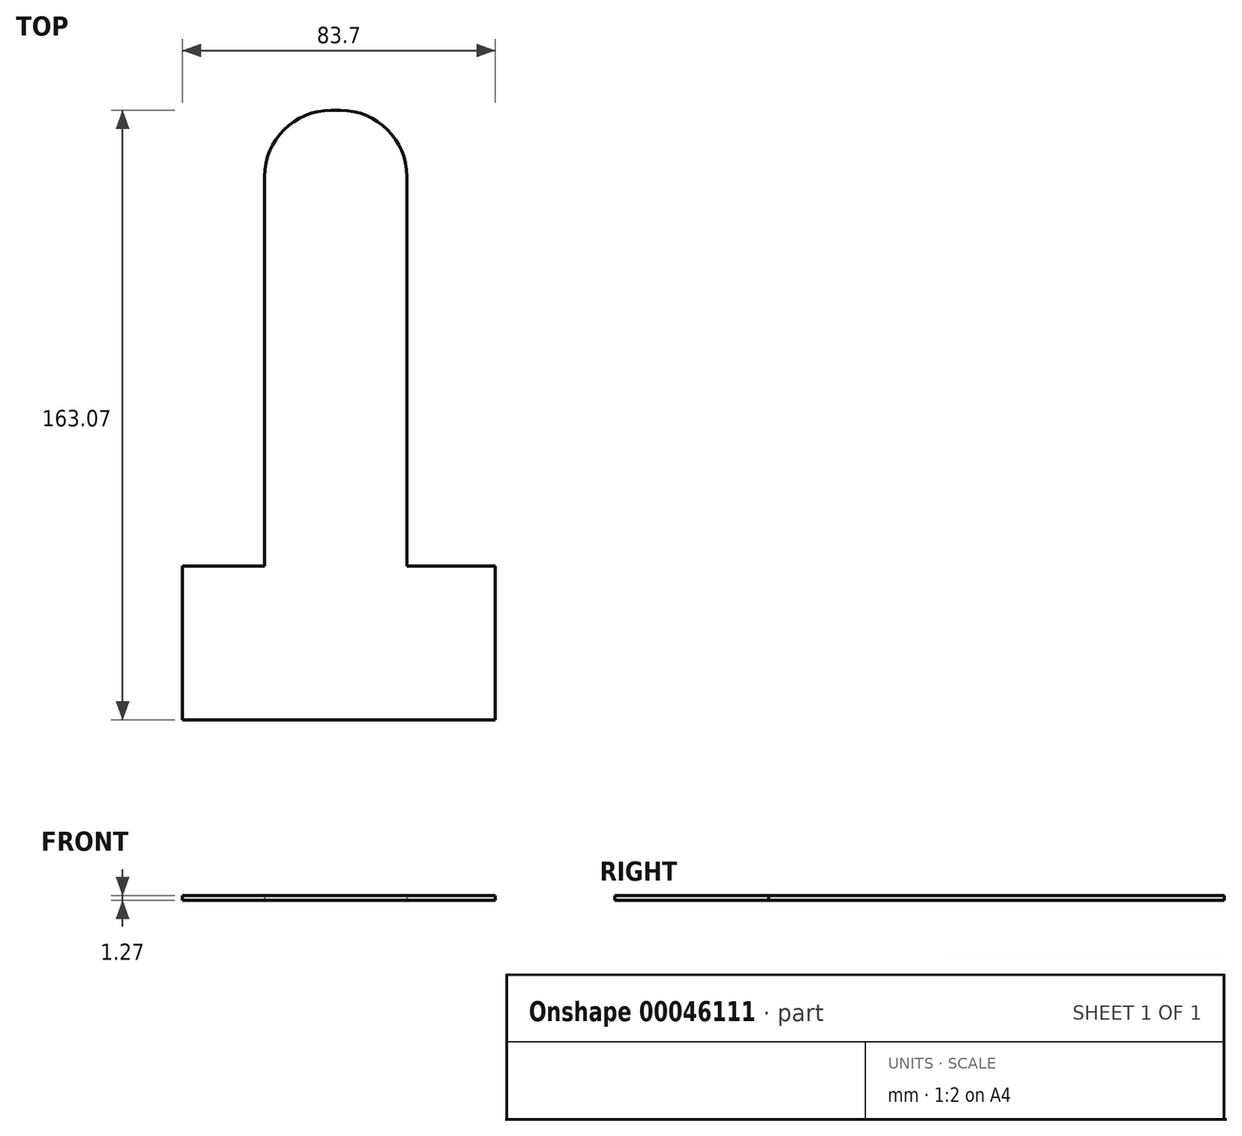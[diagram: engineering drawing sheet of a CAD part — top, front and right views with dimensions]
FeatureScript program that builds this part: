
annotation { "Feature Type Name" : "Feature", "Feature Type Description" : "" }
export const myFeature = defineFeature(function(context is Context, id is Id, definition is map)
    precondition{}
    {
        {
            var Q0;
            Q0=qCreatedBy(makeId("Top.planeOp"),FACE);
            var sketch = newSketch(context, id + "F0", { "sketchPlane" : qUnion([Q0])});
            skLineSegment(sketch, "E0", {"start": v(-41.7, -21.85) * mm, "end": v(42, -21.85) * mm});
            skLineSegment(sketch, "E1", {"start": v(-19.71, 141.22) * mm, "end": v(-19.71, 19.3) * mm});
            skLineSegment(sketch, "E2", {"start": v(18.39, 19.3) * mm, "end": v(18.39, 141.22) * mm});
            skLineSegment(sketch, "E3", {"start": v(18.39, 141.22) * mm, "end": v(-19.71, 141.22) * mm});
            skLineSegment(sketch, "E4", {"start": v(-41.7, -21.85) * mm, "end": v(-41.7, 19.3) * mm});
            skLineSegment(sketch, "E5", {"start": v(42, 19.3) * mm, "end": v(42, -21.85) * mm});
            skLineSegment(sketch, "E6", {"start": v(-41.7, 19.3) * mm, "end": v(-19.71, 19.3) * mm});
            skLineSegment(sketch, "E7", {"start": v(18.39, 19.3) * mm, "end": v(42, 19.3) * mm});
            skSolve(sketch);
        }
        {
            var Q0;
            Q0 = qSketchRegion(id + "F0", true);
            extrude(context, id + "F1", {"entities" : qUnion([Q0]), "depth" : 1.27 * mm});
        }
        {
            var Q0;
            Q0=makeQuery(id+"F1.opExtrude","SWEPT_EDGE",EDGE,{"disambiguationData":[OSD([sQuery(id+"F0.wireOp",EDGE,"E1"),sQuery(id+"F0.wireOp",EDGE,"E3")])]});
            var Q1;
            Q1=makeQuery(id+"F1.opExtrude","SWEPT_EDGE",EDGE,{"disambiguationData":[OSD([sQuery(id+"F0.wireOp",EDGE,"E2"),sQuery(id+"F0.wireOp",EDGE,"E3")])]});
            fillet(context, id + "F2", {"entities" : qUnion([Q0, Q1]), "radius" : 17.78 * mm, "tangentPropagation" : true, "allowEdgeOverflow" : false});
        }
    });
